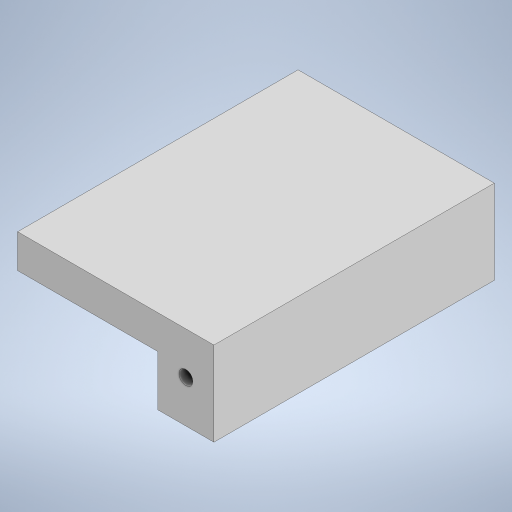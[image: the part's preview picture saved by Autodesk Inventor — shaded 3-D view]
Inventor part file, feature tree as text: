
AUTODESK INVENTOR PART (.ipt)
format: ipt  version: 2023 (Build 270158000, 158)  size: 226,816 bytes
history: native  units: in
note: dims shown in document units (in); Inventor stores cm internally (conversion verified against a paired STEP export)
features: extrude x3, sketch x3
ambient origin geometry x8: Origin, YZ Plane, XZ Plane, XY Plane, X Axis, Y Axis, Z Axis, Center Point
bodies: Body1 (feature_tree)
feature tree (6):
  extrude  "Extrusion2"  Depth=0.7874in
  extrude  "Extrusion5"  Depth=0.3937in
  extrude  "Extrusion7"  Depth=0.9843in TaperAngle=0.0deg
  sketch  "Sketch1"  dims[d0=1.1811in d1=0.7874in]
  sketch  "Sketch5"  dims[d5=0.3937in d6=0.5906in]
  sketch  "Sketch7"  dims[d7=0.1969in d8=0.9843in d9=0.0in d17=0.3543in d18=2.9528in d19=0.0in d25=1.9685in d26=0.4724in d27=3.937in d28=0.0in]
